# Revit family: Стол модульный Арт 20369
name_source: partatom
category: Антураж
revit_build: Autodesk Revit 2018 (Build: 20180423_1000(x64)
units: mm (PartAtom-declared; Revit-internal decimal feet)

## family parameters
Всегда вертикально = Да
Источник визуального образа = Геометрия семейства
На основе рабочей плоскости = Нет
Общий = Нет
При загрузке вырезать с полостями = Нет
Точка расчета площади = Нет

## types (3) — shared parameters
URL = https://hobbyka.ru
Артикул товара = Арт. 20369
Высота = 750 мм
Группа модели = Уличные столы
Изготовитель = ООО «Хоббика»
Материал изделия = Сталь, дерево
Ширина = 1900 мм

## per-type parameters (varying)
| type | Длина | Изображение типоразмера | Модуль 1 | Модуль 2 | Модуль 3 |
| Стол модульный. Модуль 1 | 2000 мм | Стол модульный Арт 20369 Модуль 1.jpg | Да | Нет | Нет |
| Стол модульный. Модуль 2 | 2200 мм | Стол модульный Арт 20369 Модуль 2.jpg | Нет | Да | Нет |
| Стол модульный. Модуль 3 | 2400 мм | Стол модульный Арт 20369 Модуль 3.jpg | Нет | Нет | Да |

note: column(s) folded — value = type name in every type: Описание
